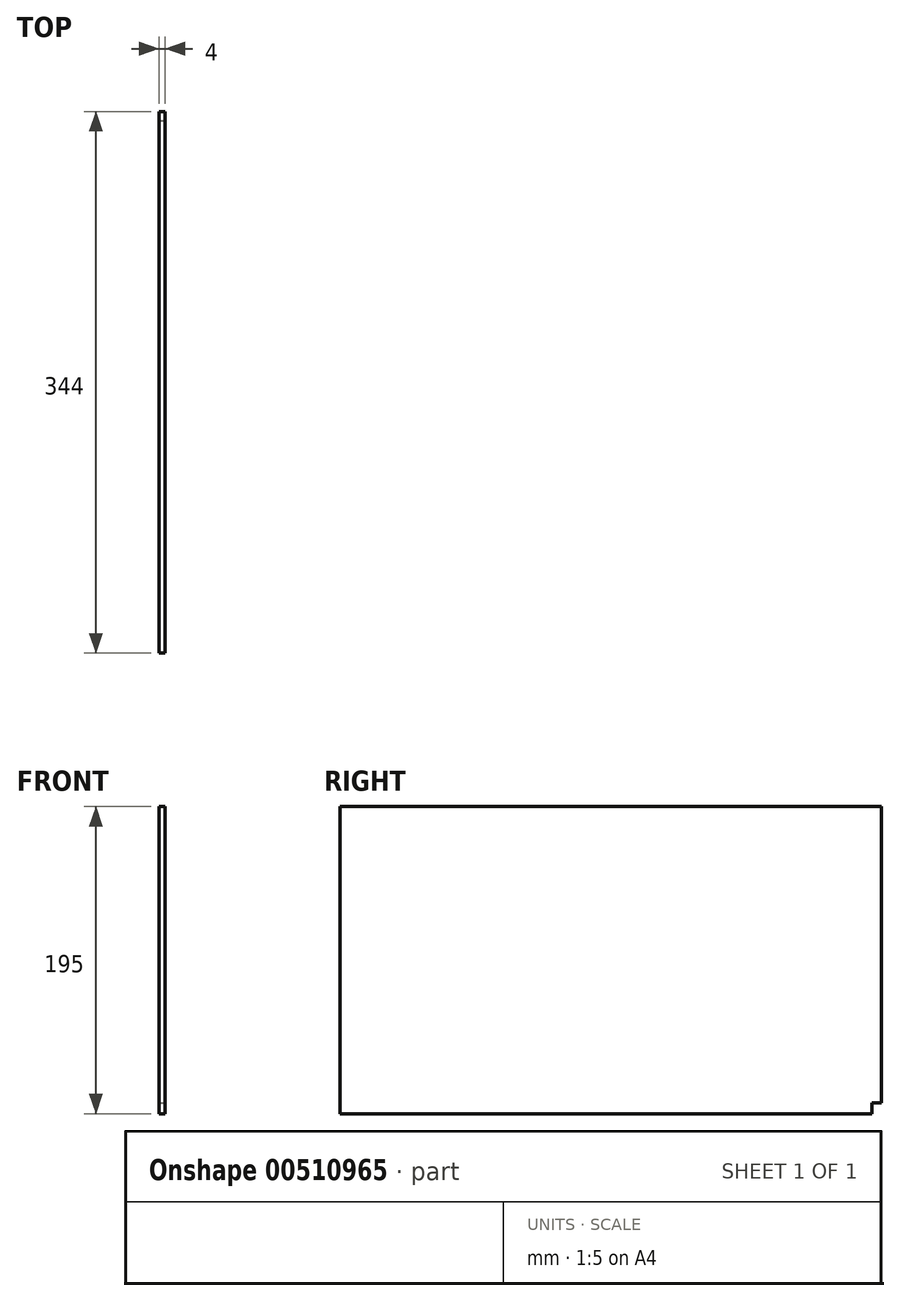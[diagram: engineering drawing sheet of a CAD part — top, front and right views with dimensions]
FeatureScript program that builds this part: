
annotation { "Feature Type Name" : "Feature", "Feature Type Description" : "" }
export const myFeature = defineFeature(function(context is Context, id is Id, definition is map)
    precondition{}
    {
        {
            var Q0;
            Q0=qCreatedBy(makeId("Right.planeOp"),FACE);
            var sketch = newSketch(context, id + "F0", { "sketchPlane" : qUnion([Q0])});
            skLineSegment(sketch, "E0.bottom", {"start": v(175, 97.5) * mm, "end": v(-175, 97.5) * mm});
            skLineSegment(sketch, "E0.top", {"start": v(175, -97.5) * mm, "end": v(-175, -97.5) * mm});
            skLineSegment(sketch, "E0.left", {"start": v(175, 97.5) * mm, "end": v(175, -97.5) * mm});
            skLineSegment(sketch, "E0.right", {"start": v(-175, 97.5) * mm, "end": v(-175, -97.5) * mm});
            skPoint(sketch, "E0.middle", {"position": v(0, 0) * mm});
            skLineSegment(sketch, "E1.bottom", {"start": v(175, -97.5) * mm, "end": v(163, -97.5) * mm});
            skLineSegment(sketch, "E1.top", {"start": v(175, -90.5) * mm, "end": v(163, -90.5) * mm});
            skLineSegment(sketch, "E1.left", {"start": v(175, -97.5) * mm, "end": v(175, -90.5) * mm});
            skLineSegment(sketch, "E1.right", {"start": v(163, -97.5) * mm, "end": v(163, -90.5) * mm});
            skSolve(sketch);
        }
        {
            var Q0;
            Q0=makeQuery(id+"F0.imprint","IMPRINT",FACE,{"disambiguationData":[TD([[makeQuery(id+"F0.imprint","IMPRINT",EDGE,{"derivedFrom":sQuery(id+"F0.wireOp",EDGE,"E0.bottom")}),1.0]])]});
            extrude(context, id + "F1", {"entities" : qUnion([Q0]), "depth" : 4 * mm});
        }
        {
            var Q0;
            Q0=makeQuery(id+"F1.opExtrude","CAP_FACE",FACE,{"disambiguationData":[OSD([sQuery(id+"F0.wireOp",EDGE,"E0.bottom"),sQuery(id+"F0.wireOp",EDGE,"E0.top"),sQuery(id+"F0.wireOp",EDGE,"E0.left"),sQuery(id+"F0.wireOp",EDGE,"E0.right"),sQuery(id+"F0.wireOp",EDGE,"E1.top"),sQuery(id+"F0.wireOp",EDGE,"E1.right")])],"isStart":false});
            var sketch = newSketch(context, id + "F2", { "sketchPlane" : qUnion([Q0])});
            skLineSegment(sketch, "E2.bottom", {"start": v(175, 97.5) * mm, "end": v(169, 97.5) * mm});
            skLineSegment(sketch, "E2.top", {"start": v(175, -90.5) * mm, "end": v(169, -90.5) * mm});
            skLineSegment(sketch, "E2.left", {"start": v(175, 97.5) * mm, "end": v(175, -90.5) * mm});
            skLineSegment(sketch, "E2.right", {"start": v(169, 97.5) * mm, "end": v(169, -90.5) * mm});
            skSolve(sketch);
        }
        {
            var Q0;
            Q0=makeQuery(id+"F2.imprint","IMPRINT",FACE,{"disambiguationData":[TD([[makeQuery(id+"F2.imprint","IMPRINT",EDGE,{"derivedFrom":sQuery(id+"F2.wireOp",EDGE,"E2.bottom")}),1.0]])]});
            extrude(context, id + "F3", {"entities" : qUnion([Q0]), "operationType" : NewBodyOperationType.REMOVE, "oppositeDirection" : true, "depth" : 25 * mm});
        }
    });
